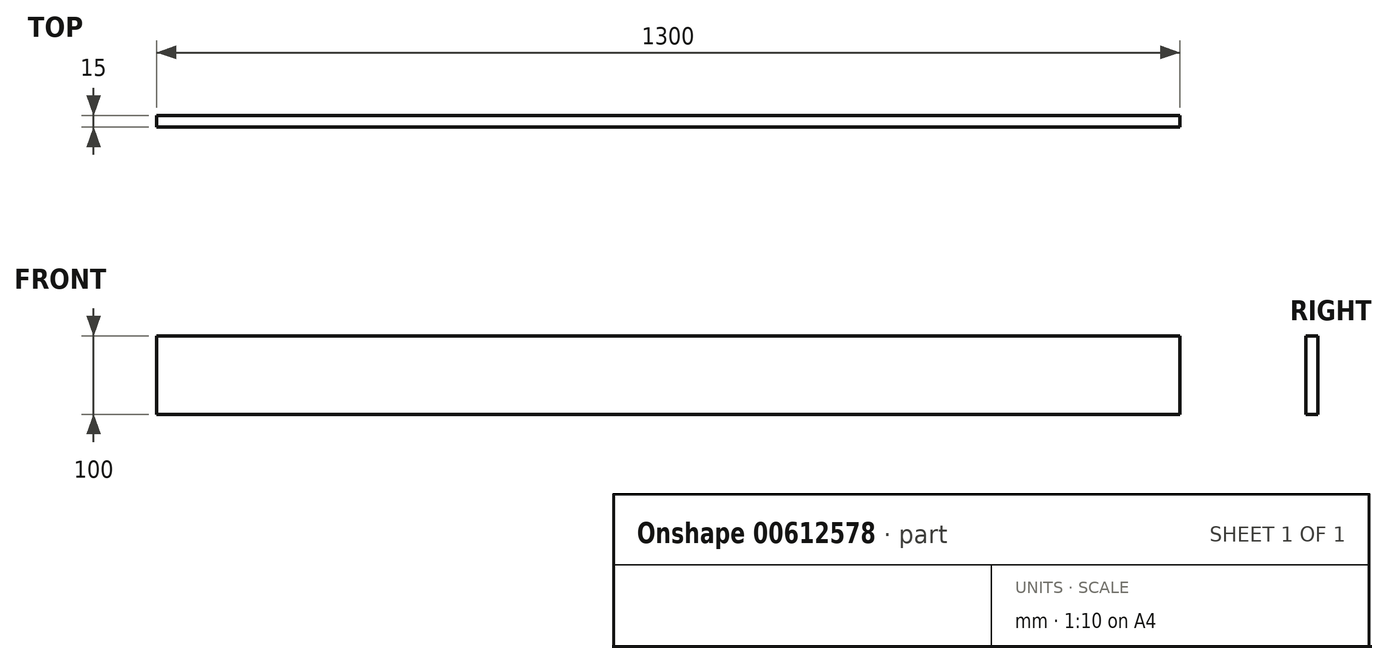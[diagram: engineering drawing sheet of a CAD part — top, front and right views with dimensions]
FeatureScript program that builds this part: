
annotation { "Feature Type Name" : "Feature", "Feature Type Description" : "" }
export const myFeature = defineFeature(function(context is Context, id is Id, definition is map)
    precondition{}
    {
        {
            var Q0;
            Q0=qCreatedBy(makeId("Front.planeOp"),FACE);
            var sketch = newSketch(context, id + "F0", { "sketchPlane" : qUnion([Q0])});
            skLineSegment(sketch, "E0.bottom", {"start": v(-650, 50) * mm, "end": v(650, 50) * mm});
            skLineSegment(sketch, "E0.top", {"start": v(-650, -50) * mm, "end": v(650, -50) * mm});
            skLineSegment(sketch, "E0.left", {"start": v(-650, 50) * mm, "end": v(-650, -50) * mm});
            skLineSegment(sketch, "E0.right", {"start": v(650, 50) * mm, "end": v(650, -50) * mm});
            skPoint(sketch, "E0.middle", {"position": v(0, 0) * mm});
            skSolve(sketch);
        }
        {
            var Q0;
            Q0=makeQuery(id+"F0.imprint","IMPRINT",FACE,{"disambiguationData":[TD([[makeQuery(id+"F0.imprint","IMPRINT",EDGE,{"derivedFrom":sQuery(id+"F0.wireOp",EDGE,"E0.bottom")}),-1.0]])]});
            extrude(context, id + "F1", {"entities" : qUnion([Q0]), "depth" : 15 * mm, "offsetDistance" : 25.4 * mm});
        }
    });
